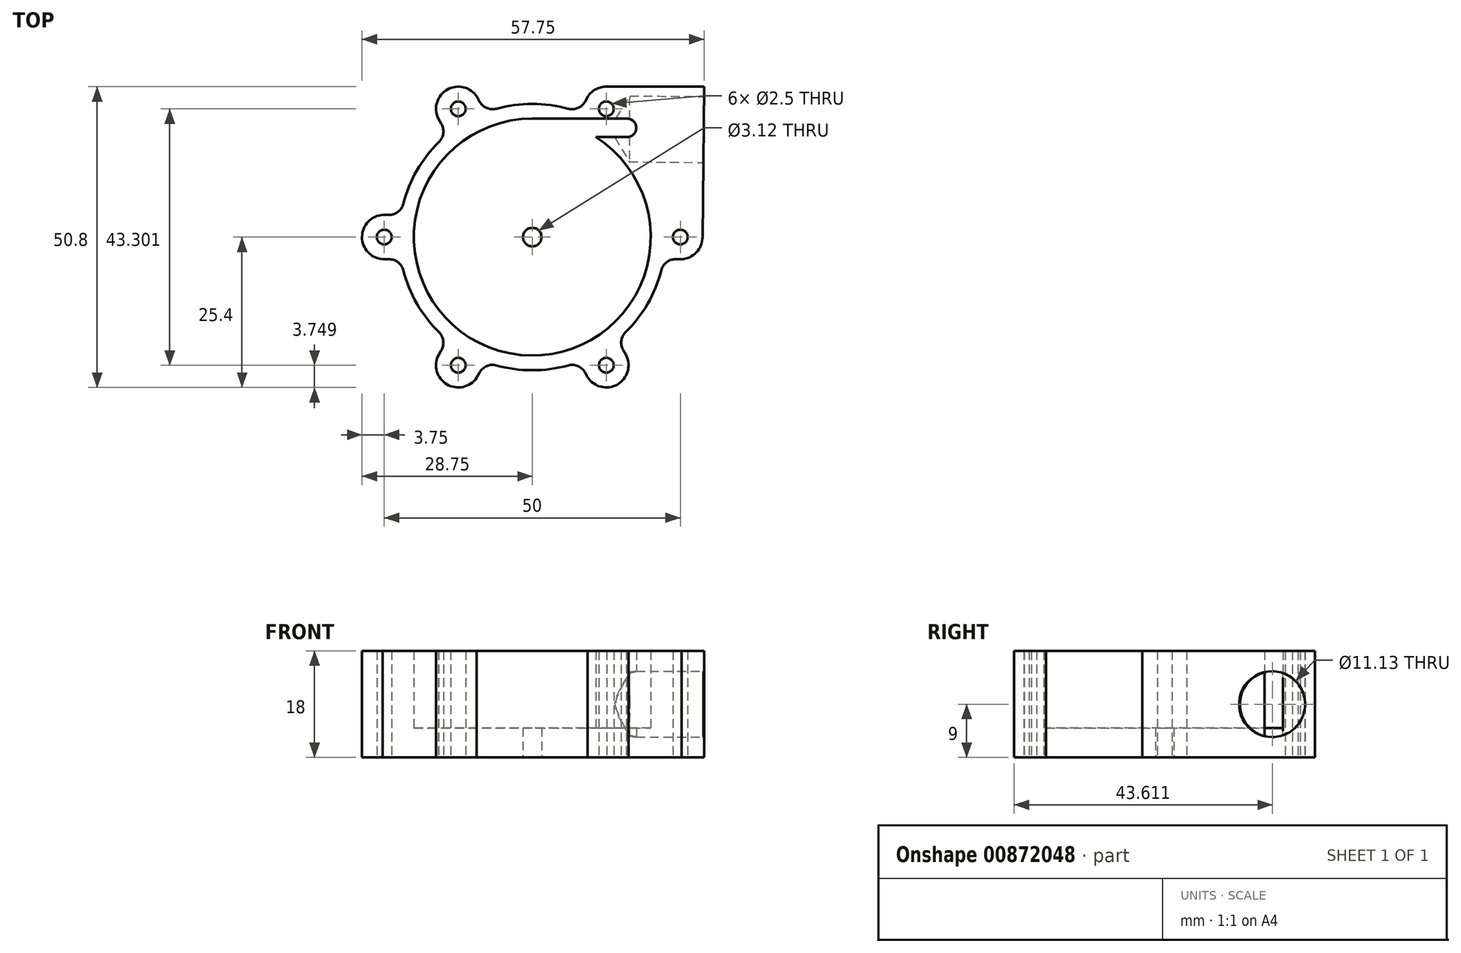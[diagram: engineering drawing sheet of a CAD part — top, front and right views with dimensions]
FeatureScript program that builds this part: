
annotation { "Feature Type Name" : "Feature", "Feature Type Description" : "" }
export const myFeature = defineFeature(function(context is Context, id is Id, definition is map)
    precondition{}
    {
        {
            var Q0;
            Q0=qCreatedBy(makeId("Top.planeOp"),FACE);
            var sketch = newSketch(context, id + "F0", { "sketchPlane" : qUnion([Q0])});
            skCircle(sketch, "E0", {"center": v(0, 0) * mm, "radius": 20 * mm});
            skArc(sketch, "E1", {"start": v(-15.76, 16.06) * mm, "mid": v(-19.48, 11.25) * mm, "end": v(-21.79, 5.62) * mm});
            skLineSegment(sketch, "E2", {"start": v(16, 20) * mm, "end": v(0, 20) * mm});
            skLineSegment(sketch, "E3", {"start": v(12.8, 18.44) * mm, "end": v(16, 18.44) * mm, "construction": true});
            skLineSegment(sketch, "E4", {"start": v(16, 24.07) * mm, "end": v(16, 20) * mm, "construction": true});
            skLineSegment(sketch, "E5", {"start": v(16, 24.07) * mm, "end": v(13.68, 20) * mm});
            skLineSegment(sketch, "E6", {"start": v(13.7, 16.87) * mm, "end": v(16, 12.95) * mm});
            skCircle(sketch, "E7", {"center": v(12.5, 21.65) * mm, "radius": 1.25 * mm});
            skLineSegment(sketch, "E8", {"start": v(12.5, 21.65) * mm, "end": v(0, 0) * mm, "construction": true});
            skCircle(sketch, "E9.1.0", {"center": v(-12.5, 21.65) * mm, "radius": 1.25 * mm});
            skCircle(sketch, "E9.2.0", {"center": v(-25, 0) * mm, "radius": 1.25 * mm});
            skCircle(sketch, "E9.3.0", {"center": v(-12.5, -21.65) * mm, "radius": 1.25 * mm});
            skCircle(sketch, "E9.4.0", {"center": v(12.5, -21.65) * mm, "radius": 1.25 * mm});
            skCircle(sketch, "E9.5.0", {"center": v(25, 0) * mm, "radius": 1.25 * mm});
            skArc(sketch, "E10", {"start": v(-9.16, 23.36) * mm, "mid": v(-14.4, 24.88) * mm, "end": v(-15.6, 19.55) * mm});
            skCircle(sketch, "E11", {"center": v(0, 0) * mm, "radius": 3.75 * mm});
            skLineSegment(sketch, "E12", {"start": v(-9.35, 23.69) * mm, "end": v(-8.86, 22.84) * mm});
            skLineSegment(sketch, "E13", {"start": v(-15.87, 20.01) * mm, "end": v(-15.34, 19.1) * mm});
            skLineSegment(sketch, "E14.trimOffspring", {"start": v(2.16, 3.75) * mm, "end": v(3.25, 1.88) * mm});
            skPoint(sketch, "E15.visualSharp", {"position": v(-7.85, 21.09) * mm});
            skArc(sketch, "E15.filletArc", {"start": v(-8.86, 22.84) * mm, "mid": v(-7.64, 21.77) * mm, "end": v(-6.03, 21.68) * mm});
            skPoint(sketch, "E16.visualSharp", {"position": v(-14.33, 17.34) * mm});
            skArc(sketch, "E16.filletArc", {"start": v(-15.76, 16.06) * mm, "mid": v(-15.03, 17.5) * mm, "end": v(-15.34, 19.1) * mm});
            skArc(sketch, "E17.1.0", {"start": v(-24.2, 3.75) * mm, "mid": v(-22.68, 4.27) * mm, "end": v(-21.79, 5.62) * mm});
            skArc(sketch, "E17.1.1", {"start": v(-21.79, -5.62) * mm, "mid": v(-22.68, -4.27) * mm, "end": v(-24.2, -3.74) * mm});
            skLineSegment(sketch, "E17.1.2", {"start": v(-25.27, -3.74) * mm, "end": v(-24.2, -3.74) * mm});
            skLineSegment(sketch, "E17.1.3", {"start": v(-25.2, 3.75) * mm, "end": v(-24.2, 3.75) * mm});
            skArc(sketch, "E17.1.4", {"start": v(-24.8, 3.75) * mm, "mid": v(-28.75, -0.04) * mm, "end": v(-24.74, -3.74) * mm});
            skArc(sketch, "E17.2.0", {"start": v(-15.35, -19.1) * mm, "mid": v(-15.04, -17.5) * mm, "end": v(-15.76, -16.06) * mm});
            skArc(sketch, "E17.2.1", {"start": v(-6.03, -21.68) * mm, "mid": v(-7.64, -21.77) * mm, "end": v(-8.86, -22.83) * mm});
            skLineSegment(sketch, "E17.2.2", {"start": v(-9.4, -23.75) * mm, "end": v(-8.86, -22.83) * mm});
            skLineSegment(sketch, "E17.2.3", {"start": v(-15.84, -19.94) * mm, "end": v(-15.35, -19.1) * mm});
            skArc(sketch, "E17.2.4", {"start": v(-15.65, -19.61) * mm, "mid": v(-14.34, -24.92) * mm, "end": v(-9.13, -23.3) * mm});
            skArc(sketch, "E17.3.0", {"start": v(8.86, -22.84) * mm, "mid": v(7.64, -21.77) * mm, "end": v(6.03, -21.68) * mm});
            skArc(sketch, "E17.3.1", {"start": v(15.76, -16.06) * mm, "mid": v(15.03, -17.5) * mm, "end": v(15.34, -19.1) * mm});
            skLineSegment(sketch, "E17.3.2", {"start": v(15.87, -20.01) * mm, "end": v(15.34, -19.1) * mm});
            skLineSegment(sketch, "E17.3.3", {"start": v(9.35, -23.69) * mm, "end": v(8.86, -22.84) * mm});
            skArc(sketch, "E17.3.4", {"start": v(9.16, -23.36) * mm, "mid": v(14.4, -24.88) * mm, "end": v(15.6, -19.55) * mm});
            skArc(sketch, "E17.4.0", {"start": v(24.2, -3.75) * mm, "mid": v(22.68, -4.27) * mm, "end": v(21.79, -5.62) * mm});
            skLineSegment(sketch, "E17.4.3", {"start": v(25.2, -3.75) * mm, "end": v(24.2, -3.75) * mm});
            skArc(sketch, "E17.4.4", {"start": v(24.8, -3.75) * mm, "mid": v(27.57, -2.73) * mm, "end": v(28.75, -0.04) * mm});
            skArc(sketch, "E17.5.1", {"start": v(6.03, 21.68) * mm, "mid": v(7.64, 21.77) * mm, "end": v(8.86, 22.83) * mm});
            skLineSegment(sketch, "E17.5.2", {"start": v(9.4, 23.75) * mm, "end": v(8.86, 22.83) * mm});
            skLineSegment(sketch, "E18", {"start": v(12.58, 25.4) * mm, "end": v(29, 25.4) * mm});
            skLineSegment(sketch, "E19", {"start": v(28.75, -0.04) * mm, "end": v(29, 25.4) * mm});
            skPoint(sketch, "E19.startSnap0", {"position": v(28.75, 0.04) * mm});
            skArc(sketch, "E20.trimOffspring", {"start": v(12.9, 18.44) * mm, "mid": v(12.86, 18.46) * mm, "end": v(12.82, 18.49) * mm});
            skArc(sketch, "E21.trimOffspring", {"start": v(12.58, 25.4) * mm, "mid": v(10.55, 24.85) * mm, "end": v(9.13, 23.3) * mm});
            skPoint(sketch, "E22.orphan", {"position": v(15.35, 19.1) * mm});
            skArc(sketch, "E23.trimOffspring", {"start": v(6.03, 21.68) * mm, "mid": v(0, 22.5) * mm, "end": v(-6.03, 21.68) * mm});
            skPoint(sketch, "E24.orphan", {"position": v(24.2, 3.74) * mm});
            skArc(sketch, "E25.trimOffspring", {"start": v(-21.79, -5.62) * mm, "mid": v(-19.49, -11.25) * mm, "end": v(-15.76, -16.06) * mm});
            skArc(sketch, "E26.trimOffspring", {"start": v(-6.03, -21.68) * mm, "mid": v(0, -22.5) * mm, "end": v(6.03, -21.68) * mm});
            skArc(sketch, "E27.trimOffspring", {"start": v(15.76, -16.06) * mm, "mid": v(19.48, -11.25) * mm, "end": v(21.79, -5.62) * mm});
            skLineSegment(sketch, "E28.trimOffspring", {"start": v(10.73, 16.88) * mm, "end": v(16, 16.87) * mm});
            skPoint(sketch, "E29.end.orphan", {"position": v(0, 16.88) * mm});
            skPoint(sketch, "E30.orphan", {"position": v(0, 18.44) * mm});
            skArc(sketch, "E31", {"start": v(16, 16.87) * mm, "mid": v(17.56, 18.44) * mm, "end": v(16, 20) * mm});
            skLineSegment(sketch, "E32.trimOffspring", {"start": v(16, 16.87) * mm, "end": v(16, 12.95) * mm, "construction": true});
            skLineSegment(sketch, "E33.trimOffspring", {"start": v(12.82, 18.49) * mm, "end": v(12.8, 18.44) * mm});
            skSolve(sketch);
        }
        {
            var Q0;
            Q0=makeQuery(id+"F0.imprint","IMPRINT",FACE,{"disambiguationData":[TD([[makeQuery(id+"F0.imprint","IMPRINT",EDGE,{"derivedFrom":sQuery(id+"F0.wireOp",EDGE,"E1")}),1.0]])]});
            extrude(context, id + "F1", {"entities" : qUnion([Q0]), "depth" : 18 * mm, "offsetDistance" : 25 * mm});
        }
        {
            var Q0;
            Q0=makeQuery(id+"F1.opExtrude","SWEPT_FACE",FACE,{"disambiguationData":[OSD([sQuery(id+"F0.wireOp",EDGE,"E19")])]});
            var sketch = newSketch(context, id + "F2", { "sketchPlane" : qUnion([Q0])});
            skCircle(sketch, "E34", {"center": v(18.43, 9) * mm, "radius": 5.57 * mm});
            skSolve(sketch);
        }
        {
            var Q0;
            Q0=sQuery(id+"F2.wireOp",VERTEX,"E34.center");
            var Q1;
            Q1=makeQuery(id+"F1.opExtrude","SWEPT_BODY",BODY,{"disambiguationData":[OSD([sQuery(id+"F0.wireOp",EDGE,"E0"),sQuery(id+"F0.wireOp",EDGE,"E1"),sQuery(id+"F0.wireOp",EDGE,"E2"),sQuery(id+"F0.wireOp",EDGE,"E7"),sQuery(id+"F0.wireOp",EDGE,"E9.1.0"),sQuery(id+"F0.wireOp",EDGE,"E9.2.0"),sQuery(id+"F0.wireOp",EDGE,"E9.3.0"),sQuery(id+"F0.wireOp",EDGE,"E9.4.0"),sQuery(id+"F0.wireOp",EDGE,"E9.5.0"),sQuery(id+"F0.wireOp",EDGE,"E10"),sQuery(id+"F0.wireOp",EDGE,"E12"),sQuery(id+"F0.wireOp",EDGE,"E13"),sQuery(id+"F0.wireOp",EDGE,"E15.filletArc"),sQuery(id+"F0.wireOp",EDGE,"E16.filletArc"),sQuery(id+"F0.wireOp",EDGE,"E17.1.0"),sQuery(id+"F0.wireOp",EDGE,"E17.1.1"),sQuery(id+"F0.wireOp",EDGE,"E17.1.2"),sQuery(id+"F0.wireOp",EDGE,"E17.1.3"),sQuery(id+"F0.wireOp",EDGE,"E17.1.4"),sQuery(id+"F0.wireOp",EDGE,"E17.2.0"),sQuery(id+"F0.wireOp",EDGE,"E17.2.1"),sQuery(id+"F0.wireOp",EDGE,"E17.2.2"),sQuery(id+"F0.wireOp",EDGE,"E17.2.3"),sQuery(id+"F0.wireOp",EDGE,"E17.2.4"),sQuery(id+"F0.wireOp",EDGE,"E17.3.0"),sQuery(id+"F0.wireOp",EDGE,"E17.3.1"),sQuery(id+"F0.wireOp",EDGE,"E17.3.2"),sQuery(id+"F0.wireOp",EDGE,"E17.3.3"),sQuery(id+"F0.wireOp",EDGE,"E17.3.4"),sQuery(id+"F0.wireOp",EDGE,"E17.4.0"),sQuery(id+"F0.wireOp",EDGE,"E17.4.3"),sQuery(id+"F0.wireOp",EDGE,"E17.4.4"),sQuery(id+"F0.wireOp",EDGE,"E17.5.1"),sQuery(id+"F0.wireOp",EDGE,"E17.5.2"),sQuery(id+"F0.wireOp",EDGE,"E18"),sQuery(id+"F0.wireOp",EDGE,"E19"),sQuery(id+"F0.wireOp",EDGE,"E21.trimOffspring"),sQuery(id+"F0.wireOp",EDGE,"E23.trimOffspring"),sQuery(id+"F0.wireOp",EDGE,"E25.trimOffspring"),sQuery(id+"F0.wireOp",EDGE,"E26.trimOffspring"),sQuery(id+"F0.wireOp",EDGE,"E27.trimOffspring"),sQuery(id+"F0.wireOp",EDGE,"E28.trimOffspring"),sQuery(id+"F0.wireOp",EDGE,"E31")])]});
            hole(context, id + "F3", {"style" : HoleStyle.SIMPLE, "endStyle" : HoleEndStyle.BLIND, "holeDiameter" : 11.13 * mm, "majorDiameter" : 5 * mm, "holeDepth" : 12.5 * mm, "isTappedThrough" : true, "tappedDepth" : 12 * mm, "tapClearance" : 3, "startFromSketch" : true, "locations" : qUnion([Q0]), "scope" : qUnion([Q1])});
        }
        {
            var Q0;
            Q0=makeQuery(id+"F1.opExtrude","CAP_FACE",FACE,{"disambiguationData":[OSD([sQuery(id+"F0.wireOp",EDGE,"E0"),sQuery(id+"F0.wireOp",EDGE,"E1"),sQuery(id+"F0.wireOp",EDGE,"E2"),sQuery(id+"F0.wireOp",EDGE,"E7"),sQuery(id+"F0.wireOp",EDGE,"E9.1.0"),sQuery(id+"F0.wireOp",EDGE,"E9.2.0"),sQuery(id+"F0.wireOp",EDGE,"E9.3.0"),sQuery(id+"F0.wireOp",EDGE,"E9.4.0"),sQuery(id+"F0.wireOp",EDGE,"E9.5.0"),sQuery(id+"F0.wireOp",EDGE,"E10"),sQuery(id+"F0.wireOp",EDGE,"E12"),sQuery(id+"F0.wireOp",EDGE,"E13"),sQuery(id+"F0.wireOp",EDGE,"E15.filletArc"),sQuery(id+"F0.wireOp",EDGE,"E16.filletArc"),sQuery(id+"F0.wireOp",EDGE,"E17.1.0"),sQuery(id+"F0.wireOp",EDGE,"E17.1.1"),sQuery(id+"F0.wireOp",EDGE,"E17.1.2"),sQuery(id+"F0.wireOp",EDGE,"E17.1.3"),sQuery(id+"F0.wireOp",EDGE,"E17.1.4"),sQuery(id+"F0.wireOp",EDGE,"E17.2.0"),sQuery(id+"F0.wireOp",EDGE,"E17.2.1"),sQuery(id+"F0.wireOp",EDGE,"E17.2.2"),sQuery(id+"F0.wireOp",EDGE,"E17.2.3"),sQuery(id+"F0.wireOp",EDGE,"E17.2.4"),sQuery(id+"F0.wireOp",EDGE,"E17.3.0"),sQuery(id+"F0.wireOp",EDGE,"E17.3.1"),sQuery(id+"F0.wireOp",EDGE,"E17.3.2"),sQuery(id+"F0.wireOp",EDGE,"E17.3.3"),sQuery(id+"F0.wireOp",EDGE,"E17.3.4"),sQuery(id+"F0.wireOp",EDGE,"E17.4.0"),sQuery(id+"F0.wireOp",EDGE,"E17.4.3"),sQuery(id+"F0.wireOp",EDGE,"E17.4.4"),sQuery(id+"F0.wireOp",EDGE,"E17.5.1"),sQuery(id+"F0.wireOp",EDGE,"E17.5.2"),sQuery(id+"F0.wireOp",EDGE,"E18"),sQuery(id+"F0.wireOp",EDGE,"E19"),sQuery(id+"F0.wireOp",EDGE,"E21.trimOffspring"),sQuery(id+"F0.wireOp",EDGE,"E23.trimOffspring"),sQuery(id+"F0.wireOp",EDGE,"E25.trimOffspring"),sQuery(id+"F0.wireOp",EDGE,"E26.trimOffspring"),sQuery(id+"F0.wireOp",EDGE,"E27.trimOffspring"),sQuery(id+"F0.wireOp",EDGE,"E28.trimOffspring"),sQuery(id+"F0.wireOp",EDGE,"E31")])],"isStart":true});
            var sketch = newSketch(context, id + "F4", { "sketchPlane" : qUnion([Q0])});
            skArc(sketch, "E35.0", {"start": v(0, -20) * mm, "mid": v(-5.6, 19.2) * mm, "end": v(10.73, -16.88) * mm});
            skLineSegment(sketch, "E36.0", {"start": v(10.73, -16.88) * mm, "end": v(16, -16.87) * mm});
            skLineSegment(sketch, "E37.0", {"start": v(16, -20) * mm, "end": v(0, -20) * mm});
            skArc(sketch, "E38.0", {"start": v(16, -16.87) * mm, "mid": v(17.56, -18.44) * mm, "end": v(16, -20) * mm});
            skCircle(sketch, "E39", {"center": v(0, 0) * mm, "radius": 1.56 * mm});
            skSolve(sketch);
        }
        {
            var Q0;
            Q0=makeQuery(id+"F4.imprint","IMPRINT",FACE,{"disambiguationData":[TD([[makeQuery(id+"F4.imprint","IMPRINT",EDGE,{"derivedFrom":sQuery(id+"F4.wireOp",EDGE,"E35.0")}),-1.0]])]});
            extrude(context, id + "F5", {"entities" : qUnion([Q0]), "operationType" : NewBodyOperationType.ADD, "oppositeDirection" : true, "depth" : 5 * mm, "offsetDistance" : 25 * mm});
        }
    });
